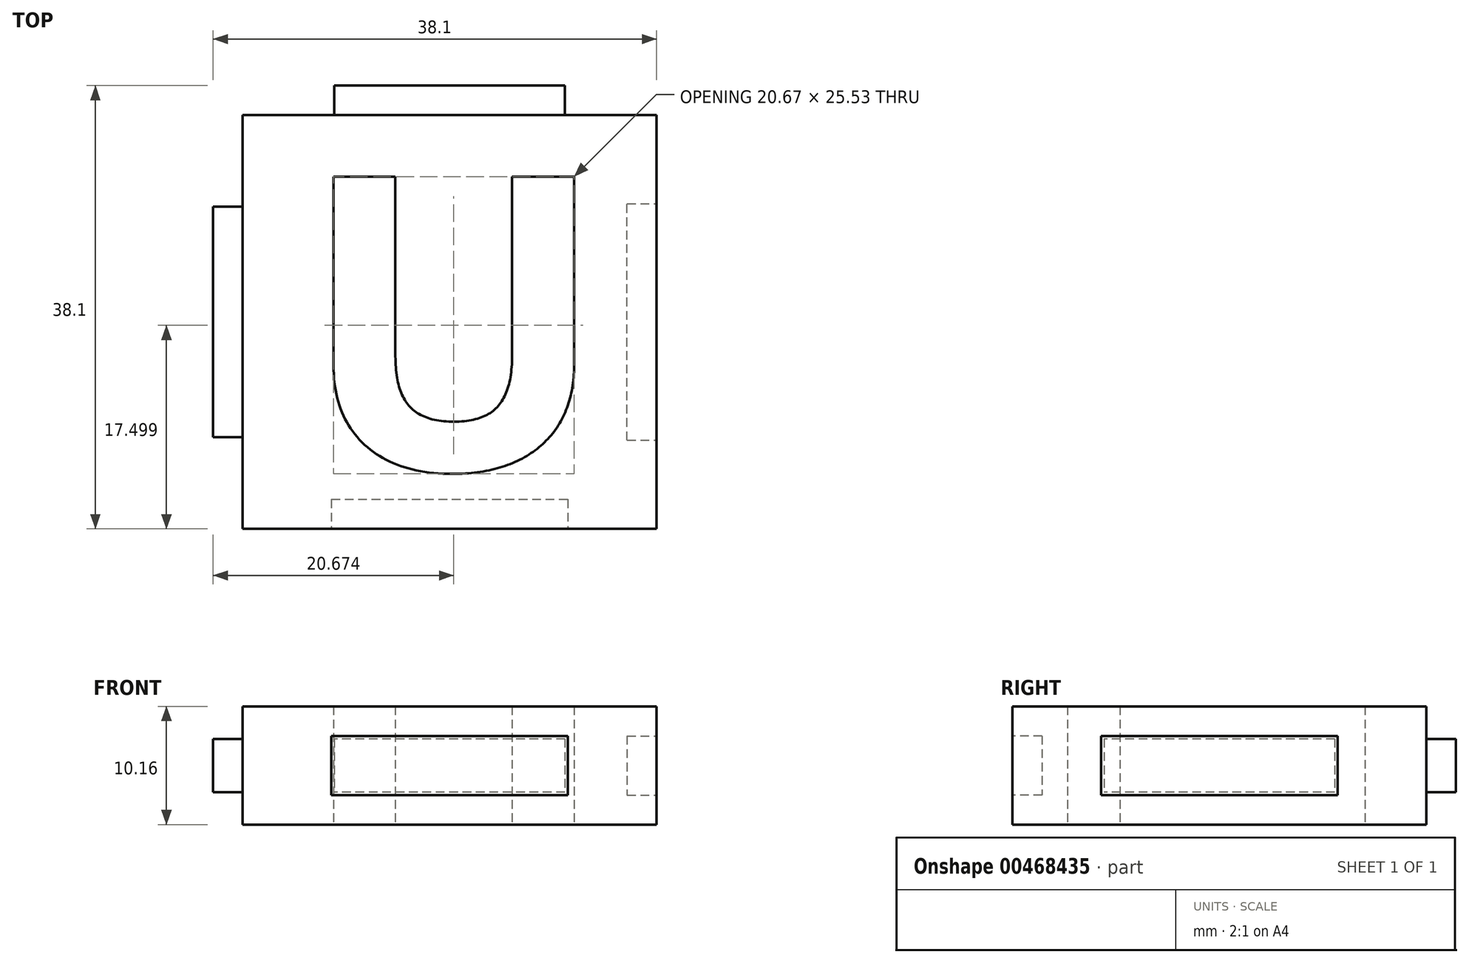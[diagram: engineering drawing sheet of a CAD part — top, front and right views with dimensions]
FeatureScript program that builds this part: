
annotation { "Feature Type Name" : "Feature", "Feature Type Description" : "" }
export const myFeature = defineFeature(function(context is Context, id is Id, definition is map)
    precondition{}
    {
        {
            var Q0;
            Q0=qCreatedBy(makeId("Top.planeOp"),FACE);
            var sketch = newSketch(context, id + "F0", { "sketchPlane" : qUnion([Q0])});
            skLineSegment(sketch, "E0.bottom", {"start": v(-17.78, 17.78) * mm, "end": v(17.78, 17.78) * mm});
            skLineSegment(sketch, "E0.top", {"start": v(-17.78, -17.78) * mm, "end": v(17.78, -17.78) * mm});
            skLineSegment(sketch, "E0.left", {"start": v(-17.78, 17.78) * mm, "end": v(-17.78, -17.78) * mm});
            skLineSegment(sketch, "E0.right", {"start": v(17.78, 17.78) * mm, "end": v(17.78, -17.78) * mm});
            skText(sketch, "E1", { "text": "U", "fontName": "OpenSans-Bold.ttf"});
            const initialGuessF0  = {"E1": [-0.01298, -0.0127, 1, 0, 0.0254]};
            skSetInitialGuess(sketch, initialGuessF0);
            skSolve(sketch);
        }
        {
            var Q0;
            Q0=qSketchRegion(id+"F0",true);
            extrude(context, id + "F1", {"entities" : qUnion([Q0]), "endBound" : BoundingType.SYMMETRIC, "depth" : 10.16 * mm});
        }
        {
            var Q0;
            Q0=makeQuery(id+"F1.opExtrude","SWEPT_FACE",FACE,{"disambiguationData":[OSD([sQuery(id+"F0.wireOp",EDGE,"E0.bottom")])]});
            var sketch = newSketch(context, id + "F2", { "sketchPlane" : qUnion([Q0])});
            skLineSegment(sketch, "E2.bottom", {"start": v(-9.9, 2.29) * mm, "end": v(9.9, 2.29) * mm});
            skLineSegment(sketch, "E2.top", {"start": v(-9.9, -2.29) * mm, "end": v(9.9, -2.29) * mm});
            skLineSegment(sketch, "E2.left", {"start": v(-9.9, 2.29) * mm, "end": v(-9.9, -2.29) * mm});
            skLineSegment(sketch, "E2.right", {"start": v(9.9, 2.29) * mm, "end": v(9.9, -2.29) * mm});
            skSolve(sketch);
        }
        {
            var Q0;
            Q0=qSketchRegion(id+"F2",true);
            extrude(context, id + "F3", {"entities" : qUnion([Q0]), "operationType" : NewBodyOperationType.ADD, "depth" : 2.54 * mm});
        }
        {
            var Q0;
            Q0=makeQuery(id+"F1.opExtrude","SWEPT_FACE",FACE,{"disambiguationData":[OSD([sQuery(id+"F0.wireOp",EDGE,"E0.left")])]});
            var sketch = newSketch(context, id + "F4", { "sketchPlane" : qUnion([Q0])});
            skLineSegment(sketch, "E3.bottom", {"start": v(-9.9, 2.29) * mm, "end": v(9.9, 2.29) * mm});
            skLineSegment(sketch, "E3.top", {"start": v(-9.9, -2.29) * mm, "end": v(9.9, -2.29) * mm});
            skLineSegment(sketch, "E3.left", {"start": v(-9.9, 2.29) * mm, "end": v(-9.9, -2.29) * mm});
            skLineSegment(sketch, "E3.right", {"start": v(9.9, 2.29) * mm, "end": v(9.9, -2.29) * mm});
            skSolve(sketch);
        }
        {
            var Q0;
            Q0=qSketchRegion(id+"F4",true);
            extrude(context, id + "F5", {"entities" : qUnion([Q0]), "operationType" : NewBodyOperationType.ADD, "depth" : 2.54 * mm});
        }
        {
            var Q0;
            Q0=makeQuery(id+"F1.opExtrude","SWEPT_FACE",FACE,{"disambiguationData":[OSD([sQuery(id+"F0.wireOp",EDGE,"E0.top")])]});
            var sketch = newSketch(context, id + "F6", { "sketchPlane" : qUnion([Q0])});
            skLineSegment(sketch, "E4.bottom", {"start": v(-10.16, 2.54) * mm, "end": v(10.16, 2.54) * mm});
            skLineSegment(sketch, "E4.top", {"start": v(-10.16, -2.54) * mm, "end": v(10.16, -2.54) * mm});
            skLineSegment(sketch, "E4.left", {"start": v(-10.16, 2.54) * mm, "end": v(-10.16, -2.54) * mm});
            skLineSegment(sketch, "E4.right", {"start": v(10.16, 2.54) * mm, "end": v(10.16, -2.54) * mm});
            skSolve(sketch);
        }
        {
            var Q0;
            Q0=qSketchRegion(id+"F6",true);
            extrude(context, id + "F7", {"entities" : qUnion([Q0]), "operationType" : NewBodyOperationType.REMOVE, "oppositeDirection" : true, "depth" : 2.54 * mm});
        }
        {
            var Q0;
            Q0=makeQuery(id+"F1.opExtrude","SWEPT_FACE",FACE,{"disambiguationData":[OSD([sQuery(id+"F0.wireOp",EDGE,"E0.right")])]});
            var sketch = newSketch(context, id + "F8", { "sketchPlane" : qUnion([Q0])});
            skLineSegment(sketch, "E5.bottom", {"start": v(-10.16, 2.54) * mm, "end": v(10.16, 2.54) * mm});
            skLineSegment(sketch, "E5.top", {"start": v(-10.16, -2.54) * mm, "end": v(10.16, -2.54) * mm});
            skLineSegment(sketch, "E5.left", {"start": v(-10.16, 2.54) * mm, "end": v(-10.16, -2.54) * mm});
            skLineSegment(sketch, "E5.right", {"start": v(10.16, 2.54) * mm, "end": v(10.16, -2.54) * mm});
            skSolve(sketch);
        }
        {
            var Q0;
            Q0=qSketchRegion(id+"F8",true);
            extrude(context, id + "F9", {"entities" : qUnion([Q0]), "operationType" : NewBodyOperationType.REMOVE, "oppositeDirection" : true, "depth" : 2.54 * mm});
        }
    });
